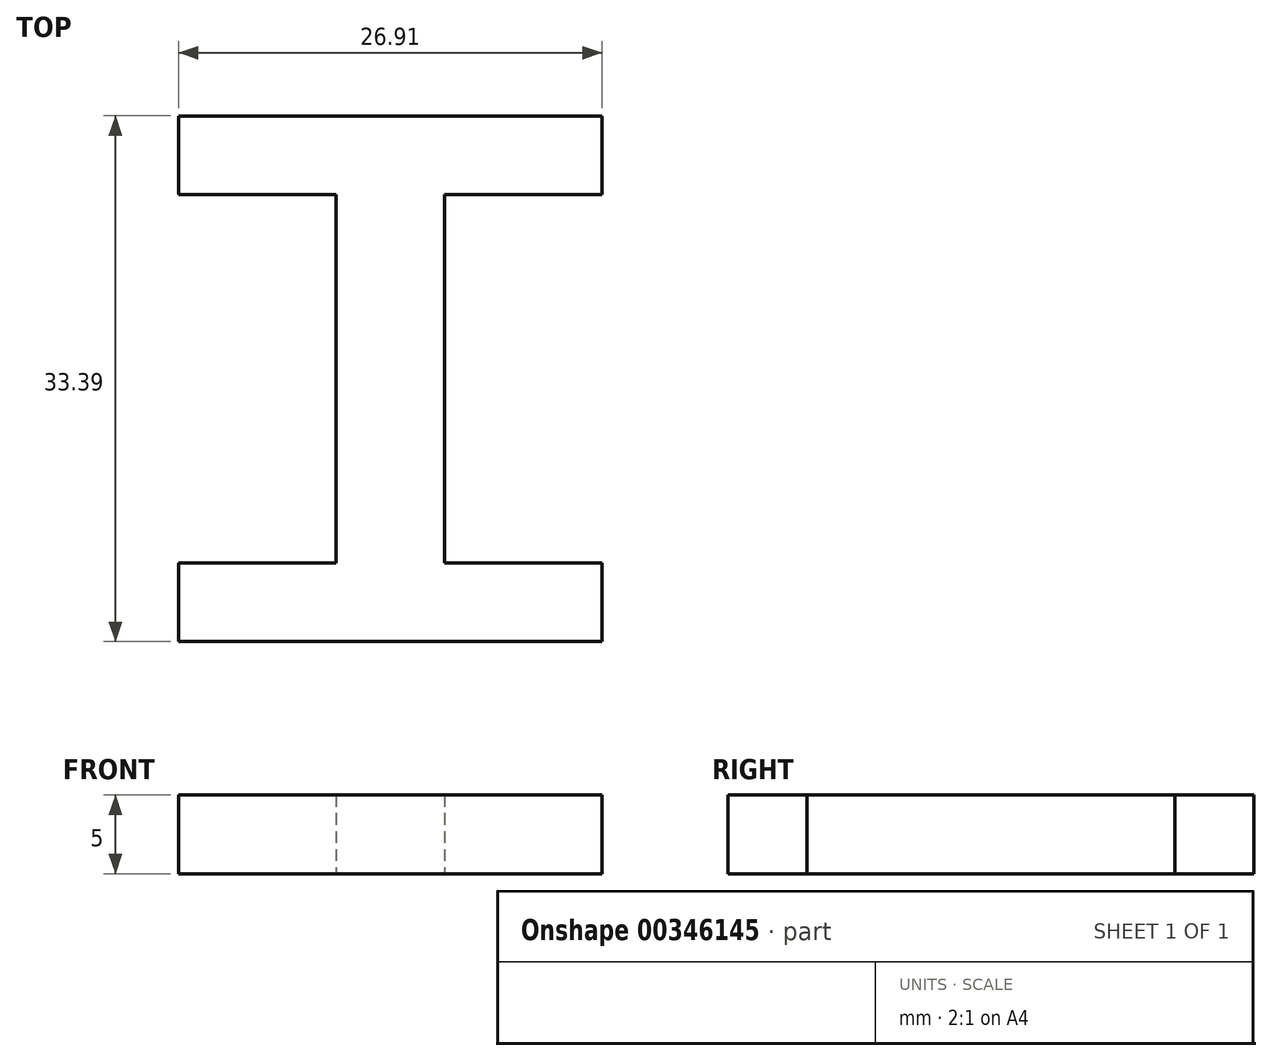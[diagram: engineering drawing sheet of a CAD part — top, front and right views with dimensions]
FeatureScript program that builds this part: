
annotation { "Feature Type Name" : "Feature", "Feature Type Description" : "" }
export const myFeature = defineFeature(function(context is Context, id is Id, definition is map)
    precondition{}
    {
        {
            var Q0;
            Q0=qCreatedBy(makeId("Top.planeOp"),FACE);
            var sketch = newSketch(context, id + "F0", { "sketchPlane" : qUnion([Q0])});
            skLineSegment(sketch, "E0", {"start": v(0, 0) * mm, "end": v(0, 33.39) * mm});
            skLineSegment(sketch, "E1", {"start": v(0, 33.39) * mm, "end": v(6.9, 33.39) * mm});
            skLineSegment(sketch, "E2", {"start": v(6.9, 33.39) * mm, "end": v(6.9, 0) * mm});
            skLineSegment(sketch, "E3", {"start": v(6.9, 0) * mm, "end": v(0, 0) * mm});
            skSolve(sketch);
        }
        {
            var Q0;
            Q0 = qSketchRegion(id + "F0", true);
            extrude(context, id + "F1", {"entities" : qUnion([Q0]), "depth" : 5 * mm});
        }
        {
            var Q0;
            Q0=qCreatedBy(makeId("Top.planeOp"),FACE);
            var sketch = newSketch(context, id + "F2", { "sketchPlane" : qUnion([Q0])});
            skLineSegment(sketch, "E4.0.0", {"start": v(0, 0) * mm, "end": v(6.9, 0) * mm});
            skLineSegment(sketch, "E4.0.1", {"start": v(6.9, 0) * mm, "end": v(6.9, 33.39) * mm});
            skLineSegment(sketch, "E4.0.2", {"start": v(6.9, 33.39) * mm, "end": v(0, 33.39) * mm});
            skLineSegment(sketch, "E4.0.3", {"start": v(0, 33.39) * mm, "end": v(0, 0) * mm});
            skLineSegment(sketch, "E5", {"start": v(0, 0) * mm, "end": v(-9.34, 0) * mm});
            skLineSegment(sketch, "E6", {"start": v(-9.34, 0) * mm, "end": v(-9.34, 5) * mm});
            skLineSegment(sketch, "E7", {"start": v(-9.34, 5) * mm, "end": v(0, 5) * mm});
            skLineSegment(sketch, "E8", {"start": v(6.9, 0) * mm, "end": v(16.9, 0) * mm});
            skLineSegment(sketch, "E9", {"start": v(16.9, 0) * mm, "end": v(16.9, 4.57) * mm});
            skLineSegment(sketch, "E10", {"start": v(16.9, 4.57) * mm, "end": v(6.9, 4.57) * mm});
            skLineSegment(sketch, "E11", {"start": v(-9.34, 5) * mm, "end": v(-9.34, 0) * mm});
            skLineSegment(sketch, "E12", {"start": v(0, 33.39) * mm, "end": v(-10, 33.39) * mm});
            skLineSegment(sketch, "E13", {"start": v(-10, 33.39) * mm, "end": v(-10, 28.39) * mm});
            skLineSegment(sketch, "E14", {"start": v(-10, 28.39) * mm, "end": v(0, 28.39) * mm});
            skLineSegment(sketch, "E15", {"start": v(6.9, 33.39) * mm, "end": v(16.9, 33.39) * mm});
            skLineSegment(sketch, "E16", {"start": v(16.9, 33.39) * mm, "end": v(16.9, 28.39) * mm});
            skLineSegment(sketch, "E17", {"start": v(16.9, 28.39) * mm, "end": v(6.9, 28.39) * mm});
            skLineSegment(sketch, "E18", {"start": v(6.9, 28.39) * mm, "end": v(16.9, 28.39) * mm});
            skSolve(sketch);
        }
        {
            var Q0;
            Q0=makeQuery(id+"F1.opExtrude","CAP_FACE",FACE,{"disambiguationData":[OSD([sQuery(id+"F0.wireOp",EDGE,"E0"),sQuery(id+"F0.wireOp",EDGE,"E1"),sQuery(id+"F0.wireOp",EDGE,"E2"),sQuery(id+"F0.wireOp",EDGE,"E3")])],"isStart":true});
            var sketch = newSketch(context, id + "F3", { "sketchPlane" : qUnion([Q0])});
            skLineSegment(sketch, "E19.0.0", {"start": v(6.9, 0) * mm, "end": v(0, 0) * mm});
            skLineSegment(sketch, "E19.0.1", {"start": v(0, 0) * mm, "end": v(0, -33.39) * mm});
            skLineSegment(sketch, "E19.0.2", {"start": v(0, -33.39) * mm, "end": v(6.9, -33.39) * mm});
            skLineSegment(sketch, "E19.0.3", {"start": v(6.9, -33.39) * mm, "end": v(6.9, 0) * mm});
            skLineSegment(sketch, "E20", {"start": v(0, 0) * mm, "end": v(-10, 0) * mm});
            skLineSegment(sketch, "E21", {"start": v(-10, 0) * mm, "end": v(-10, -5) * mm});
            skLineSegment(sketch, "E22", {"start": v(-10, -5) * mm, "end": v(0, -5) * mm});
            skLineSegment(sketch, "E23", {"start": v(0, -5) * mm, "end": v(0, 0) * mm});
            skLineSegment(sketch, "E24", {"start": v(6.9, 0) * mm, "end": v(16.9, 0) * mm});
            skLineSegment(sketch, "E25", {"start": v(16.9, 0) * mm, "end": v(16.9, -5) * mm});
            skLineSegment(sketch, "E26", {"start": v(16.9, -5) * mm, "end": v(6.9, -5) * mm});
            skLineSegment(sketch, "E27", {"start": v(0, -33.39) * mm, "end": v(-10, -33.39) * mm});
            skLineSegment(sketch, "E28", {"start": v(-10, -33.39) * mm, "end": v(-10, -28.39) * mm});
            skLineSegment(sketch, "E29", {"start": v(-10, -28.39) * mm, "end": v(0, -28.39) * mm});
            skLineSegment(sketch, "E30", {"start": v(6.9, -33.39) * mm, "end": v(16.9, -33.39) * mm});
            skLineSegment(sketch, "E31", {"start": v(16.9, -33.39) * mm, "end": v(16.9, -28.39) * mm});
            skLineSegment(sketch, "E32", {"start": v(16.9, -28.39) * mm, "end": v(6.9, -28.39) * mm});
            skSolve(sketch);
        }
        {
            var Q0;
            Q0 = qSketchRegion(id + "F3", true);
            var Q1;
            {var subQ0=sQuery(id+"F2.wireOp",EDGE,"E12");Q1=makeQuery(id+"F2.imprint","IMPRINT",FACE,{"disambiguationData":[TD([[makeQuery(id+"F2.imprint","IMPRINT",EDGE,{"derivedFrom":subQ0}),1.0]])]});}
            extrude(context, id + "F4", {"entities" : qUnion([Q0, Q1]), "operationType" : NewBodyOperationType.ADD, "oppositeDirection" : true, "depth" : 5 * mm});
        }
    });
